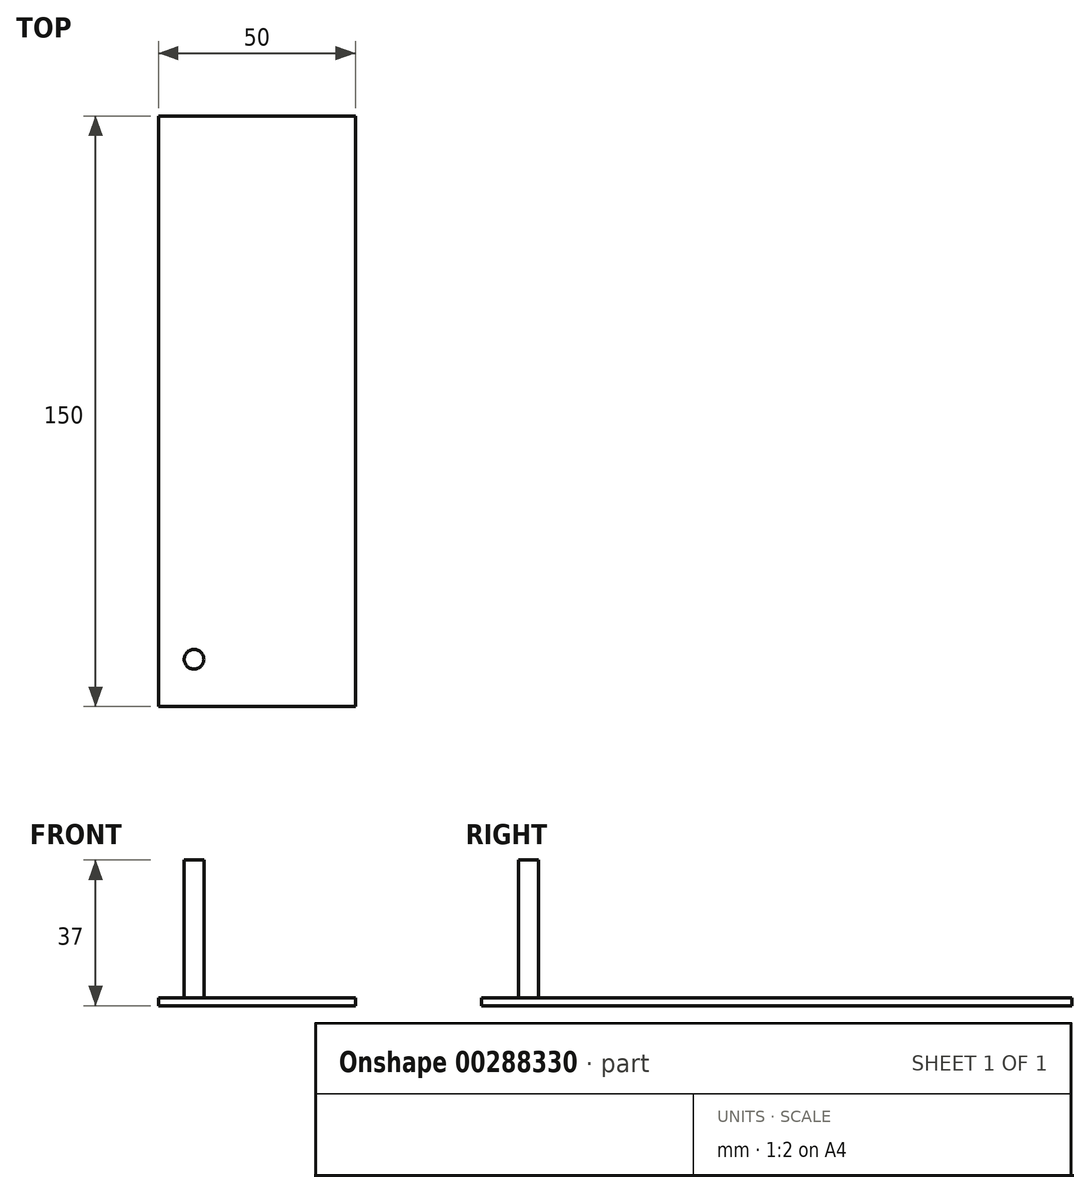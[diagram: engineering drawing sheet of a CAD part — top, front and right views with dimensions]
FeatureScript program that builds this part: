
annotation { "Feature Type Name" : "Feature", "Feature Type Description" : "" }
export const myFeature = defineFeature(function(context is Context, id is Id, definition is map)
    precondition{}
    {
        {
            var Q0;
            Q0=qCreatedBy(makeId("Top.planeOp"),FACE);
            var sketch = newSketch(context, id + "F0", { "sketchPlane" : qUnion([Q0])});
            skLineSegment(sketch, "E0.bottom", {"start": v(25, -75) * mm, "end": v(-25, -75) * mm});
            skLineSegment(sketch, "E0.top", {"start": v(25, 75) * mm, "end": v(-25, 75) * mm});
            skLineSegment(sketch, "E0.left", {"start": v(25, -75) * mm, "end": v(25, 75) * mm});
            skLineSegment(sketch, "E0.right", {"start": v(-25, -75) * mm, "end": v(-25, 75) * mm});
            skPoint(sketch, "E0.middle", {"position": v(0, 0) * mm});
            skSolve(sketch);
        }
        {
            var Q0;
            Q0 = qSketchRegion(id + "F0", true);
            extrude(context, id + "F1", {"entities" : qUnion([Q0]), "depth" : 2 * mm});
        }
        {
            var Q0;
            Q0=makeQuery(id+"F1.opExtrude","CAP_FACE",FACE,{"disambiguationData":[OSD([sQuery(id+"F0.wireOp",EDGE,"E0.bottom"),sQuery(id+"F0.wireOp",EDGE,"E0.top"),sQuery(id+"F0.wireOp",EDGE,"E0.left"),sQuery(id+"F0.wireOp",EDGE,"E0.right")])],"isStart":false});
            var sketch = newSketch(context, id + "F2", { "sketchPlane" : qUnion([Q0])});
            skCircle(sketch, "E1", {"center": v(-16, -63) * mm, "radius": 2.5 * mm});
            skLineSegment(sketch, "E2", {"start": v(0, 0) * mm, "end": v(0, -63) * mm, "construction": true});
            skLineSegment(sketch, "E3", {"start": v(0, -63) * mm, "end": v(-16, -63) * mm, "construction": true});
            skSolve(sketch);
        }
        {
            var Q0;
            Q0 = qSketchRegion(id + "F2", true);
            extrude(context, id + "F3", {"entities" : qUnion([Q0]), "operationType" : NewBodyOperationType.ADD, "depth" : 35 * mm});
        }
    });
